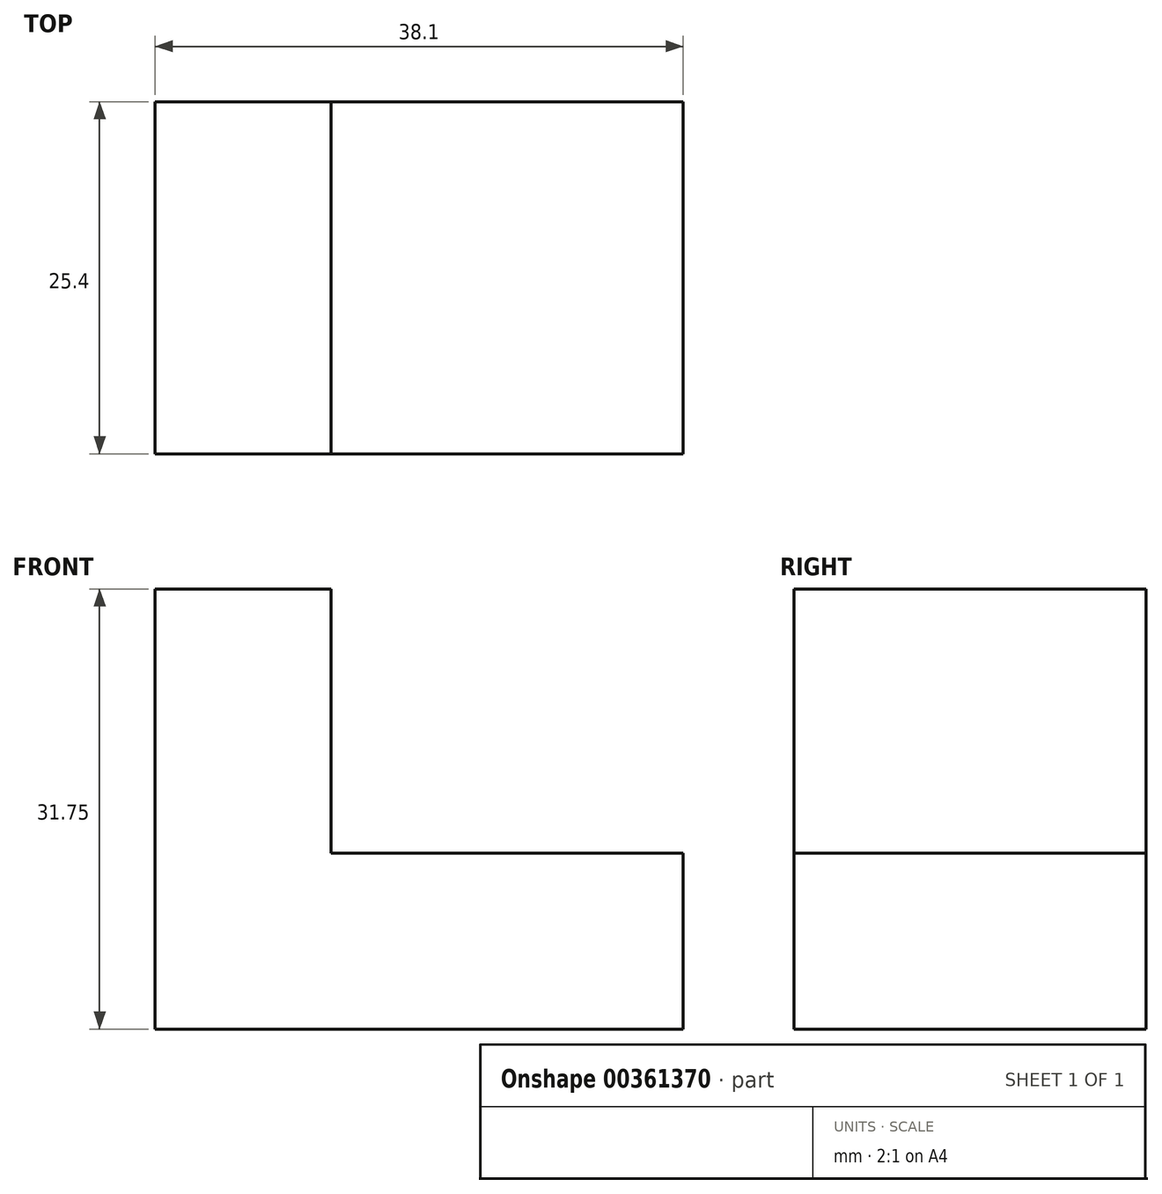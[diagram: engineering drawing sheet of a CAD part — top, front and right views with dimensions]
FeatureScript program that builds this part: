
annotation { "Feature Type Name" : "Feature", "Feature Type Description" : "" }
export const myFeature = defineFeature(function(context is Context, id is Id, definition is map)
    precondition{}
    {
        {
            var Q0;
            Q0=qCreatedBy(makeId("Front.planeOp"),FACE);
            var sketch = newSketch(context, id + "F0", { "sketchPlane" : qUnion([Q0])});
            skLineSegment(sketch, "E0", {"start": v(-51.81, 25.2) * mm, "end": v(-51.81, -6.54) * mm});
            skLineSegment(sketch, "E1", {"start": v(-51.81, -6.54) * mm, "end": v(-13.71, -6.54) * mm});
            skLineSegment(sketch, "E2", {"start": v(-13.71, -6.54) * mm, "end": v(-13.71, 6.16) * mm});
            skLineSegment(sketch, "E3", {"start": v(-13.71, 6.16) * mm, "end": v(-39.11, 6.16) * mm});
            skLineSegment(sketch, "E4", {"start": v(-39.11, 6.16) * mm, "end": v(-39.11, 25.2) * mm});
            skLineSegment(sketch, "E5", {"start": v(-39.11, 25.2) * mm, "end": v(-51.81, 25.2) * mm});
            skSolve(sketch);
        }
        {
            var Q0;
            Q0 = qSketchRegion(id + "F0", true);
            extrude(context, id + "F1", {"entities" : qUnion([Q0]), "depth" : 25.4 * mm});
        }
    });
